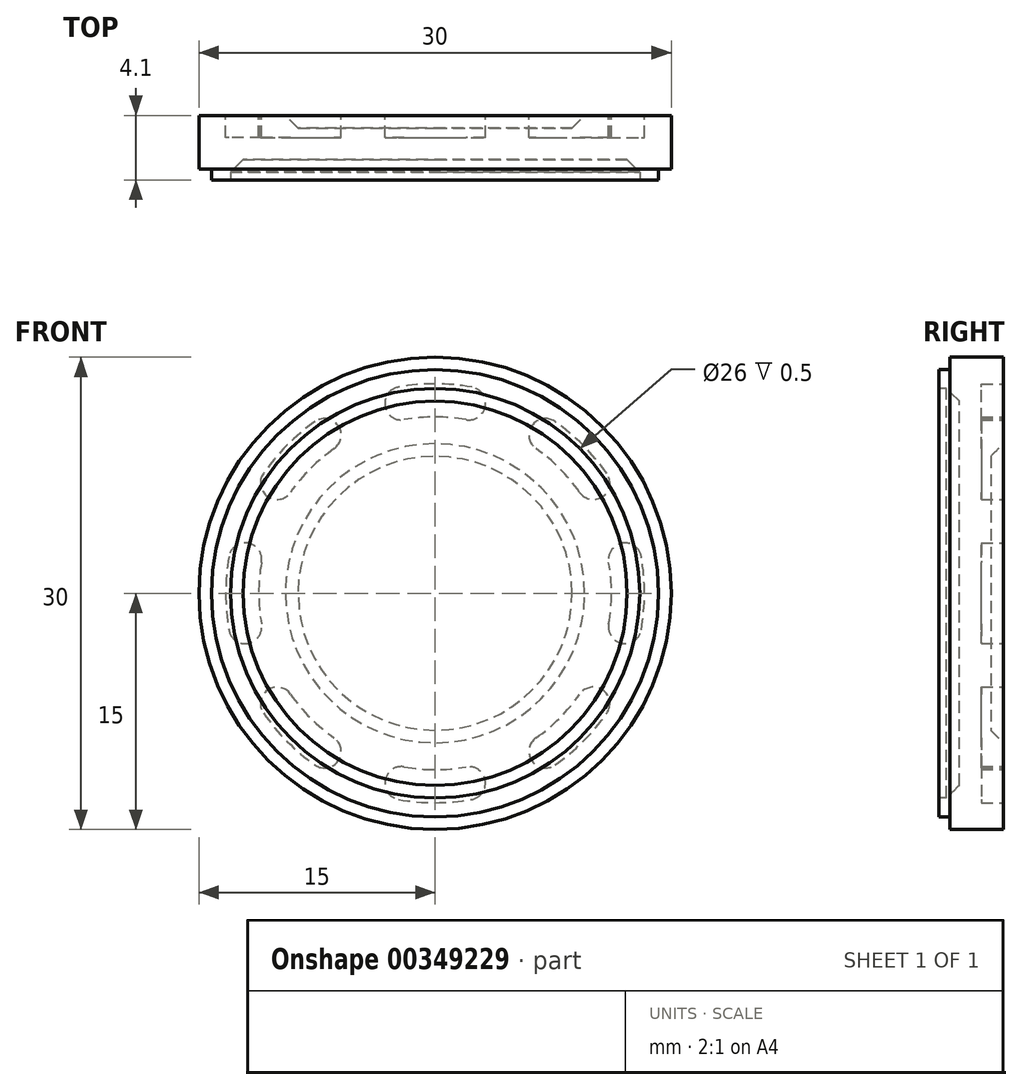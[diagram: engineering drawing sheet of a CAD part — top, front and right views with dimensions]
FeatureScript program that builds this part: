
annotation { "Feature Type Name" : "Feature", "Feature Type Description" : "" }
export const myFeature = defineFeature(function(context is Context, id is Id, definition is map)
    precondition{}
    {
        {
            var Q0;
            Q0=qCreatedBy(makeId("Front.planeOp"),FACE);
            var sketch = newSketch(context, id + "F0", { "sketchPlane" : qUnion([Q0])});
            skCircle(sketch, "E0", {"center": v(0, 0) * mm, "radius": 15 * mm});
            skCircle(sketch, "E1", {"center": v(0, 0) * mm, "radius": 9.5 * mm});
            skCircle(sketch, "E2", {"center": v(0, 0) * mm, "radius": 11.2 * mm});
            skCircle(sketch, "E3", {"center": v(0, 0) * mm, "radius": 13.3 * mm});
            skCircle(sketch, "E4", {"center": v(-12.06, 2.15) * mm, "radius": 1.05 * mm});
            skCircle(sketch, "E5", {"center": v(-12.06, -2.15) * mm, "radius": 1.05 * mm});
            skCircle(sketch, "E6.1.0", {"center": v(-10.05, -7.01) * mm, "radius": 1.05 * mm});
            skCircle(sketch, "E6.1.1", {"center": v(-7.01, -10.05) * mm, "radius": 1.05 * mm});
            skCircle(sketch, "E6.2.0", {"center": v(-2.15, -12.06) * mm, "radius": 1.05 * mm});
            skCircle(sketch, "E6.2.1", {"center": v(2.15, -12.06) * mm, "radius": 1.05 * mm});
            skCircle(sketch, "E7.1.3.0", {"center": v(7.01, -10.05) * mm, "radius": 1.05 * mm});
            skCircle(sketch, "E7.2.3.0", {"center": v(10.05, -7.01) * mm, "radius": 1.05 * mm});
            skCircle(sketch, "E7.1.4.0", {"center": v(12.06, -2.15) * mm, "radius": 1.05 * mm});
            skCircle(sketch, "E7.2.4.0", {"center": v(12.06, 2.15) * mm, "radius": 1.05 * mm});
            skCircle(sketch, "E7.1.5.0", {"center": v(10.05, 7.01) * mm, "radius": 1.05 * mm});
            skCircle(sketch, "E7.2.5.0", {"center": v(7.01, 10.05) * mm, "radius": 1.05 * mm});
            skCircle(sketch, "E7.1.6.0", {"center": v(2.15, 12.06) * mm, "radius": 1.05 * mm});
            skCircle(sketch, "E7.2.6.0", {"center": v(-2.15, 12.06) * mm, "radius": 1.05 * mm});
            skCircle(sketch, "E7.1.7.0", {"center": v(-7.01, 10.05) * mm, "radius": 1.05 * mm});
            skCircle(sketch, "E7.2.7.0", {"center": v(-10.05, 7.01) * mm, "radius": 1.05 * mm});
            skSolve(sketch);
        }
        {
            var Q0;
            Q0=qSketchRegion(id+"F0",true);
            var Q1;
            Q1=makeQuery(id+"F0.imprint","IMPRINT",FACE,{"disambiguationData":[TD([[makeQuery(id+"F0.imprint","IMPRINT",EDGE,{"derivedFrom":sQuery(id+"F0.wireOp",EDGE,"E1")}),1.0]])]});
            var Q2;
            {var subQ0=sQuery(id+"F0.wireOp",EDGE,"E2");var subQ1=sQuery(id+"F0.wireOp",EDGE,"vEkXL8x0-xW5C-LHgK-BDgQ-QKywttK1u6fH");var subQ2=makeQuery(id+"F0.imprint","INTERSECT",VERTEX,{"derivedFrom":[subQ1,subQ0]});Q2=makeQuery(id+"F0.imprint","IMPRINT",FACE,{"disambiguationData":[TD([[makeQuery(id+"F0.imprint","IMPRINT",EDGE,{"disambiguationData":[TD([[subQ2,1.0]])],"derivedFrom":subQ1}),-1.0]])]});}
            var Q3;
            {var subQ0=sQuery(id+"F0.wireOp",EDGE,"E2");var subQ1=sQuery(id+"F0.wireOp",EDGE,"6eb1e324-2513-47bc-ae3c-4e5281ed8811.10.0");var subQ2=makeQuery(id+"F0.imprint","INTERSECT",VERTEX,{"derivedFrom":[subQ1,subQ0]});Q3=makeQuery(id+"F0.imprint","IMPRINT",FACE,{"disambiguationData":[TD([[makeQuery(id+"F0.imprint","IMPRINT",EDGE,{"disambiguationData":[TD([[subQ2,1.0]])],"derivedFrom":subQ1}),-1.0]])]});}
            var Q4;
            {var subQ0=sQuery(id+"F0.wireOp",EDGE,"E2");var subQ1=sQuery(id+"F0.wireOp",EDGE,"6eb1e324-2513-47bc-ae3c-4e5281ed8811.8.0");var subQ2=makeQuery(id+"F0.imprint","INTERSECT",VERTEX,{"derivedFrom":[subQ1,subQ0]});Q4=makeQuery(id+"F0.imprint","IMPRINT",FACE,{"disambiguationData":[TD([[makeQuery(id+"F0.imprint","IMPRINT",EDGE,{"disambiguationData":[TD([[subQ2,1.0]])],"derivedFrom":subQ1}),-1.0]])]});}
            var Q5;
            {var subQ0=sQuery(id+"F0.wireOp",EDGE,"E2");var subQ1=sQuery(id+"F0.wireOp",EDGE,"6eb1e324-2513-47bc-ae3c-4e5281ed8811.6.0");var subQ2=makeQuery(id+"F0.imprint","INTERSECT",VERTEX,{"derivedFrom":[subQ1,subQ0]});Q5=makeQuery(id+"F0.imprint","IMPRINT",FACE,{"disambiguationData":[TD([[makeQuery(id+"F0.imprint","IMPRINT",EDGE,{"disambiguationData":[TD([[subQ2,1.0]])],"derivedFrom":subQ1}),-1.0]])]});}
            var Q6;
            {var subQ0=sQuery(id+"F0.wireOp",EDGE,"E2");var subQ1=sQuery(id+"F0.wireOp",EDGE,"6eb1e324-2513-47bc-ae3c-4e5281ed8811.4.0");var subQ2=makeQuery(id+"F0.imprint","INTERSECT",VERTEX,{"derivedFrom":[subQ1,subQ0]});Q6=makeQuery(id+"F0.imprint","IMPRINT",FACE,{"disambiguationData":[TD([[makeQuery(id+"F0.imprint","IMPRINT",EDGE,{"disambiguationData":[TD([[subQ2,1.0]])],"derivedFrom":subQ1}),-1.0]])]});}
            var Q7;
            {var subQ0=sQuery(id+"F0.wireOp",EDGE,"E2");var subQ1=sQuery(id+"F0.wireOp",EDGE,"6eb1e324-2513-47bc-ae3c-4e5281ed8811.2.0");var subQ2=makeQuery(id+"F0.imprint","INTERSECT",VERTEX,{"derivedFrom":[subQ1,subQ0]});Q7=makeQuery(id+"F0.imprint","IMPRINT",FACE,{"disambiguationData":[TD([[makeQuery(id+"F0.imprint","IMPRINT",EDGE,{"disambiguationData":[TD([[subQ2,1.0]])],"derivedFrom":subQ1}),-1.0]])]});}
            var Q8;
            Q8=makeQuery(id+"F0.imprint","IMPRINT",FACE,{"disambiguationData":[TD([[makeQuery(id+"F0.imprint","IMPRINT",EDGE,{"derivedFrom":sQuery(id+"F0.wireOp",EDGE,"E1")}),-1.0]])]});
            var Q9;
            {var subQ0=sQuery(id+"F0.wireOp",EDGE,"6eb1e324-2513-47bc-ae3c-4e5281ed8811.7.0");var subQ1=makeQuery(id+"F0.imprint","INTERSECT",VERTEX,{"derivedFrom":[subQ0,sQuery(id+"F0.wireOp",EDGE,"E2")]});Q9=makeQuery(id+"F0.imprint","IMPRINT",FACE,{"disambiguationData":[TD([[makeQuery(id+"F0.imprint","IMPRINT",EDGE,{"disambiguationData":[TD([[subQ1,1.0]])],"derivedFrom":subQ0}),1.0]])]});}
            var Q10;
            {var subQ0=sQuery(id+"F0.wireOp",EDGE,"E2");var subQ1=sQuery(id+"F0.wireOp",EDGE,"6eb1e324-2513-47bc-ae3c-4e5281ed8811.7.0");var subQ2=makeQuery(id+"F0.imprint","INTERSECT",VERTEX,{"derivedFrom":[subQ1,subQ0]});Q10=makeQuery(id+"F0.imprint","IMPRINT",FACE,{"disambiguationData":[TD([[makeQuery(id+"F0.imprint","IMPRINT",EDGE,{"disambiguationData":[TD([[subQ2,1.0]])],"derivedFrom":subQ1}),-1.0]])]});}
            var Q11;
            {var subQ0=sQuery(id+"F0.wireOp",EDGE,"6eb1e324-2513-47bc-ae3c-4e5281ed8811.8.0");var subQ1=makeQuery(id+"F0.imprint","INTERSECT",VERTEX,{"derivedFrom":[subQ0,sQuery(id+"F0.wireOp",EDGE,"E2")]});Q11=makeQuery(id+"F0.imprint","IMPRINT",FACE,{"disambiguationData":[TD([[makeQuery(id+"F0.imprint","IMPRINT",EDGE,{"disambiguationData":[TD([[subQ1,1.0]])],"derivedFrom":subQ0}),1.0]])]});}
            var Q12;
            {var subQ0=sQuery(id+"F0.wireOp",EDGE,"6eb1e324-2513-47bc-ae3c-4e5281ed8811.9.0");var subQ1=makeQuery(id+"F0.imprint","INTERSECT",VERTEX,{"derivedFrom":[subQ0,sQuery(id+"F0.wireOp",EDGE,"E2")]});Q12=makeQuery(id+"F0.imprint","IMPRINT",FACE,{"disambiguationData":[TD([[makeQuery(id+"F0.imprint","IMPRINT",EDGE,{"disambiguationData":[TD([[subQ1,1.0]])],"derivedFrom":subQ0}),1.0]])]});}
            var Q13;
            {var subQ0=sQuery(id+"F0.wireOp",EDGE,"E2");var subQ1=sQuery(id+"F0.wireOp",EDGE,"6eb1e324-2513-47bc-ae3c-4e5281ed8811.9.0");var subQ2=makeQuery(id+"F0.imprint","INTERSECT",VERTEX,{"derivedFrom":[subQ1,subQ0]});Q13=makeQuery(id+"F0.imprint","IMPRINT",FACE,{"disambiguationData":[TD([[makeQuery(id+"F0.imprint","IMPRINT",EDGE,{"disambiguationData":[TD([[subQ2,1.0]])],"derivedFrom":subQ1}),-1.0]])]});}
            var Q14;
            {var subQ0=sQuery(id+"F0.wireOp",EDGE,"6eb1e324-2513-47bc-ae3c-4e5281ed8811.10.0");var subQ1=makeQuery(id+"F0.imprint","INTERSECT",VERTEX,{"derivedFrom":[subQ0,sQuery(id+"F0.wireOp",EDGE,"E2")]});Q14=makeQuery(id+"F0.imprint","IMPRINT",FACE,{"disambiguationData":[TD([[makeQuery(id+"F0.imprint","IMPRINT",EDGE,{"disambiguationData":[TD([[subQ1,1.0]])],"derivedFrom":subQ0}),1.0]])]});}
            var Q15;
            {var subQ0=sQuery(id+"F0.wireOp",EDGE,"6eb1e324-2513-47bc-ae3c-4e5281ed8811.11.0");var subQ1=makeQuery(id+"F0.imprint","INTERSECT",VERTEX,{"derivedFrom":[subQ0,sQuery(id+"F0.wireOp",EDGE,"E2")]});Q15=makeQuery(id+"F0.imprint","IMPRINT",FACE,{"disambiguationData":[TD([[makeQuery(id+"F0.imprint","IMPRINT",EDGE,{"disambiguationData":[TD([[subQ1,1.0]])],"derivedFrom":subQ0}),1.0]])]});}
            var Q16;
            {var subQ0=sQuery(id+"F0.wireOp",EDGE,"E2");var subQ1=sQuery(id+"F0.wireOp",EDGE,"vEkXL8x0-xW5C-LHgK-BDgQ-QKywttK1u6fH");var subQ2=makeQuery(id+"F0.imprint","INTERSECT",VERTEX,{"derivedFrom":[subQ1,subQ0]});Q16=makeQuery(id+"F0.imprint","IMPRINT",FACE,{"disambiguationData":[TD([[makeQuery(id+"F0.imprint","IMPRINT",EDGE,{"disambiguationData":[TD([[subQ2,-1.0]])],"derivedFrom":subQ1}),-1.0]])]});}
            var Q17;
            {var subQ0=sQuery(id+"F0.wireOp",EDGE,"vEkXL8x0-xW5C-LHgK-BDgQ-QKywttK1u6fH");var subQ1=makeQuery(id+"F0.imprint","INTERSECT",VERTEX,{"derivedFrom":[subQ0,sQuery(id+"F0.wireOp",EDGE,"E2")]});Q17=makeQuery(id+"F0.imprint","IMPRINT",FACE,{"disambiguationData":[TD([[makeQuery(id+"F0.imprint","IMPRINT",EDGE,{"disambiguationData":[TD([[subQ1,1.0]])],"derivedFrom":subQ0}),1.0]])]});}
            var Q18;
            {var subQ0=sQuery(id+"F0.wireOp",EDGE,"6eb1e324-2513-47bc-ae3c-4e5281ed8811.1.0");var subQ1=makeQuery(id+"F0.imprint","INTERSECT",VERTEX,{"derivedFrom":[subQ0,sQuery(id+"F0.wireOp",EDGE,"E2")]});Q18=makeQuery(id+"F0.imprint","IMPRINT",FACE,{"disambiguationData":[TD([[makeQuery(id+"F0.imprint","IMPRINT",EDGE,{"disambiguationData":[TD([[subQ1,1.0]])],"derivedFrom":subQ0}),1.0]])]});}
            var Q19;
            {var subQ0=sQuery(id+"F0.wireOp",EDGE,"E2");var subQ1=sQuery(id+"F0.wireOp",EDGE,"6eb1e324-2513-47bc-ae3c-4e5281ed8811.1.0");var subQ2=makeQuery(id+"F0.imprint","INTERSECT",VERTEX,{"derivedFrom":[subQ1,subQ0]});Q19=makeQuery(id+"F0.imprint","IMPRINT",FACE,{"disambiguationData":[TD([[makeQuery(id+"F0.imprint","IMPRINT",EDGE,{"disambiguationData":[TD([[subQ2,1.0]])],"derivedFrom":subQ1}),-1.0]])]});}
            var Q20;
            {var subQ0=sQuery(id+"F0.wireOp",EDGE,"6eb1e324-2513-47bc-ae3c-4e5281ed8811.2.0");var subQ1=makeQuery(id+"F0.imprint","INTERSECT",VERTEX,{"derivedFrom":[subQ0,sQuery(id+"F0.wireOp",EDGE,"E2")]});Q20=makeQuery(id+"F0.imprint","IMPRINT",FACE,{"disambiguationData":[TD([[makeQuery(id+"F0.imprint","IMPRINT",EDGE,{"disambiguationData":[TD([[subQ1,1.0]])],"derivedFrom":subQ0}),1.0]])]});}
            var Q21;
            {var subQ0=sQuery(id+"F0.wireOp",EDGE,"6eb1e324-2513-47bc-ae3c-4e5281ed8811.3.0");var subQ1=makeQuery(id+"F0.imprint","INTERSECT",VERTEX,{"derivedFrom":[subQ0,sQuery(id+"F0.wireOp",EDGE,"E2")]});Q21=makeQuery(id+"F0.imprint","IMPRINT",FACE,{"disambiguationData":[TD([[makeQuery(id+"F0.imprint","IMPRINT",EDGE,{"disambiguationData":[TD([[subQ1,1.0]])],"derivedFrom":subQ0}),1.0]])]});}
            var Q22;
            {var subQ0=sQuery(id+"F0.wireOp",EDGE,"E2");var subQ1=sQuery(id+"F0.wireOp",EDGE,"6eb1e324-2513-47bc-ae3c-4e5281ed8811.3.0");var subQ2=makeQuery(id+"F0.imprint","INTERSECT",VERTEX,{"derivedFrom":[subQ1,subQ0]});Q22=makeQuery(id+"F0.imprint","IMPRINT",FACE,{"disambiguationData":[TD([[makeQuery(id+"F0.imprint","IMPRINT",EDGE,{"disambiguationData":[TD([[subQ2,1.0]])],"derivedFrom":subQ1}),-1.0]])]});}
            var Q23;
            {var subQ0=sQuery(id+"F0.wireOp",EDGE,"6eb1e324-2513-47bc-ae3c-4e5281ed8811.4.0");var subQ1=makeQuery(id+"F0.imprint","INTERSECT",VERTEX,{"derivedFrom":[subQ0,sQuery(id+"F0.wireOp",EDGE,"E2")]});Q23=makeQuery(id+"F0.imprint","IMPRINT",FACE,{"disambiguationData":[TD([[makeQuery(id+"F0.imprint","IMPRINT",EDGE,{"disambiguationData":[TD([[subQ1,1.0]])],"derivedFrom":subQ0}),1.0]])]});}
            var Q24;
            {var subQ0=sQuery(id+"F0.wireOp",EDGE,"6eb1e324-2513-47bc-ae3c-4e5281ed8811.5.0");var subQ1=makeQuery(id+"F0.imprint","INTERSECT",VERTEX,{"derivedFrom":[subQ0,sQuery(id+"F0.wireOp",EDGE,"E2")]});Q24=makeQuery(id+"F0.imprint","IMPRINT",FACE,{"disambiguationData":[TD([[makeQuery(id+"F0.imprint","IMPRINT",EDGE,{"disambiguationData":[TD([[subQ1,1.0]])],"derivedFrom":subQ0}),1.0]])]});}
            var Q25;
            {var subQ0=sQuery(id+"F0.wireOp",EDGE,"E2");var subQ1=sQuery(id+"F0.wireOp",EDGE,"6eb1e324-2513-47bc-ae3c-4e5281ed8811.5.0");var subQ2=makeQuery(id+"F0.imprint","INTERSECT",VERTEX,{"derivedFrom":[subQ1,subQ0]});Q25=makeQuery(id+"F0.imprint","IMPRINT",FACE,{"disambiguationData":[TD([[makeQuery(id+"F0.imprint","IMPRINT",EDGE,{"disambiguationData":[TD([[subQ2,1.0]])],"derivedFrom":subQ1}),-1.0]])]});}
            var Q26;
            {var subQ0=sQuery(id+"F0.wireOp",EDGE,"6eb1e324-2513-47bc-ae3c-4e5281ed8811.6.0");var subQ1=makeQuery(id+"F0.imprint","INTERSECT",VERTEX,{"derivedFrom":[subQ0,sQuery(id+"F0.wireOp",EDGE,"E2")]});Q26=makeQuery(id+"F0.imprint","IMPRINT",FACE,{"disambiguationData":[TD([[makeQuery(id+"F0.imprint","IMPRINT",EDGE,{"disambiguationData":[TD([[subQ1,1.0]])],"derivedFrom":subQ0}),1.0]])]});}
            var Q27;
            {var subQ0=sQuery(id+"F0.wireOp",EDGE,"d0c3eeaf-13b5-4f8c-83f5-547d6fbb3b3b.1.23.0");var subQ1=makeQuery(id+"F0.imprint","INTERSECT",VERTEX,{"derivedFrom":[sQuery(id+"F0.wireOp",EDGE,"E2"),subQ0]});Q27=makeQuery(id+"F0.imprint","IMPRINT",FACE,{"disambiguationData":[TD([[makeQuery(id+"F0.imprint","IMPRINT",EDGE,{"disambiguationData":[TD([[subQ1,1.0]])],"derivedFrom":subQ0}),1.0]])]});}
            var Q28;
            {var subQ0=sQuery(id+"F0.wireOp",EDGE,"d0c3eeaf-13b5-4f8c-83f5-547d6fbb3b3b.1.22.0");var subQ1=makeQuery(id+"F0.imprint","INTERSECT",VERTEX,{"derivedFrom":[sQuery(id+"F0.wireOp",EDGE,"E2"),subQ0]});Q28=makeQuery(id+"F0.imprint","IMPRINT",FACE,{"disambiguationData":[TD([[makeQuery(id+"F0.imprint","IMPRINT",EDGE,{"disambiguationData":[TD([[subQ1,1.0]])],"derivedFrom":subQ0}),1.0]])]});}
            var Q29;
            {var subQ0=sQuery(id+"F0.wireOp",EDGE,"d0c3eeaf-13b5-4f8c-83f5-547d6fbb3b3b.1.21.0");var subQ1=sQuery(id+"F0.wireOp",EDGE,"E2");var subQ2=makeQuery(id+"F0.imprint","INTERSECT",VERTEX,{"derivedFrom":[subQ1,subQ0]});Q29=makeQuery(id+"F0.imprint","IMPRINT",FACE,{"disambiguationData":[TD([[makeQuery(id+"F0.imprint","IMPRINT",EDGE,{"disambiguationData":[TD([[subQ2,-1.0]])],"derivedFrom":subQ1}),-1.0]])]});}
            var Q30;
            {var subQ0=sQuery(id+"F0.wireOp",EDGE,"d0c3eeaf-13b5-4f8c-83f5-547d6fbb3b3b.1.22.0");var subQ1=sQuery(id+"F0.wireOp",EDGE,"E2");var subQ2=makeQuery(id+"F0.imprint","INTERSECT",VERTEX,{"derivedFrom":[subQ1,subQ0]});Q30=makeQuery(id+"F0.imprint","IMPRINT",FACE,{"disambiguationData":[TD([[makeQuery(id+"F0.imprint","IMPRINT",EDGE,{"disambiguationData":[TD([[subQ2,-1.0]])],"derivedFrom":subQ1}),-1.0]])]});}
            var Q31;
            {var subQ0=sQuery(id+"F0.wireOp",EDGE,"d0c3eeaf-13b5-4f8c-83f5-547d6fbb3b3b.1.21.0");var subQ1=makeQuery(id+"F0.imprint","INTERSECT",VERTEX,{"derivedFrom":[sQuery(id+"F0.wireOp",EDGE,"E2"),subQ0]});Q31=makeQuery(id+"F0.imprint","IMPRINT",FACE,{"disambiguationData":[TD([[makeQuery(id+"F0.imprint","IMPRINT",EDGE,{"disambiguationData":[TD([[subQ1,1.0]])],"derivedFrom":subQ0}),1.0]])]});}
            var Q32;
            {var subQ0=sQuery(id+"F0.wireOp",EDGE,"d0c3eeaf-13b5-4f8c-83f5-547d6fbb3b3b.1.20.0");var subQ1=sQuery(id+"F0.wireOp",EDGE,"E2");var subQ2=makeQuery(id+"F0.imprint","INTERSECT",VERTEX,{"derivedFrom":[subQ1,subQ0]});Q32=makeQuery(id+"F0.imprint","IMPRINT",FACE,{"disambiguationData":[TD([[makeQuery(id+"F0.imprint","IMPRINT",EDGE,{"disambiguationData":[TD([[subQ2,-1.0]])],"derivedFrom":subQ1}),-1.0]])]});}
            var Q33;
            {var subQ0=sQuery(id+"F0.wireOp",EDGE,"d0c3eeaf-13b5-4f8c-83f5-547d6fbb3b3b.1.20.0");var subQ1=makeQuery(id+"F0.imprint","INTERSECT",VERTEX,{"derivedFrom":[sQuery(id+"F0.wireOp",EDGE,"E2"),subQ0]});Q33=makeQuery(id+"F0.imprint","IMPRINT",FACE,{"disambiguationData":[TD([[makeQuery(id+"F0.imprint","IMPRINT",EDGE,{"disambiguationData":[TD([[subQ1,1.0]])],"derivedFrom":subQ0}),1.0]])]});}
            var Q34;
            {var subQ0=sQuery(id+"F0.wireOp",EDGE,"d0c3eeaf-13b5-4f8c-83f5-547d6fbb3b3b.1.19.0");var subQ1=sQuery(id+"F0.wireOp",EDGE,"E2");var subQ2=makeQuery(id+"F0.imprint","INTERSECT",VERTEX,{"derivedFrom":[subQ1,subQ0]});Q34=makeQuery(id+"F0.imprint","IMPRINT",FACE,{"disambiguationData":[TD([[makeQuery(id+"F0.imprint","IMPRINT",EDGE,{"disambiguationData":[TD([[subQ2,-1.0]])],"derivedFrom":subQ1}),-1.0]])]});}
            var Q35;
            {var subQ0=sQuery(id+"F0.wireOp",EDGE,"d0c3eeaf-13b5-4f8c-83f5-547d6fbb3b3b.1.19.0");var subQ1=makeQuery(id+"F0.imprint","INTERSECT",VERTEX,{"derivedFrom":[sQuery(id+"F0.wireOp",EDGE,"E2"),subQ0]});Q35=makeQuery(id+"F0.imprint","IMPRINT",FACE,{"disambiguationData":[TD([[makeQuery(id+"F0.imprint","IMPRINT",EDGE,{"disambiguationData":[TD([[subQ1,1.0]])],"derivedFrom":subQ0}),1.0]])]});}
            var Q36;
            {var subQ0=sQuery(id+"F0.wireOp",EDGE,"d0c3eeaf-13b5-4f8c-83f5-547d6fbb3b3b.1.18.0");var subQ1=sQuery(id+"F0.wireOp",EDGE,"E2");var subQ2=makeQuery(id+"F0.imprint","INTERSECT",VERTEX,{"derivedFrom":[subQ1,subQ0]});Q36=makeQuery(id+"F0.imprint","IMPRINT",FACE,{"disambiguationData":[TD([[makeQuery(id+"F0.imprint","IMPRINT",EDGE,{"disambiguationData":[TD([[subQ2,-1.0]])],"derivedFrom":subQ1}),-1.0]])]});}
            var Q37;
            {var subQ0=sQuery(id+"F0.wireOp",EDGE,"d0c3eeaf-13b5-4f8c-83f5-547d6fbb3b3b.1.18.0");var subQ1=makeQuery(id+"F0.imprint","INTERSECT",VERTEX,{"derivedFrom":[sQuery(id+"F0.wireOp",EDGE,"E2"),subQ0]});Q37=makeQuery(id+"F0.imprint","IMPRINT",FACE,{"disambiguationData":[TD([[makeQuery(id+"F0.imprint","IMPRINT",EDGE,{"disambiguationData":[TD([[subQ1,1.0]])],"derivedFrom":subQ0}),1.0]])]});}
            var Q38;
            {var subQ0=sQuery(id+"F0.wireOp",EDGE,"d0c3eeaf-13b5-4f8c-83f5-547d6fbb3b3b.1.17.0");var subQ1=sQuery(id+"F0.wireOp",EDGE,"E2");var subQ2=makeQuery(id+"F0.imprint","INTERSECT",VERTEX,{"derivedFrom":[subQ1,subQ0]});Q38=makeQuery(id+"F0.imprint","IMPRINT",FACE,{"disambiguationData":[TD([[makeQuery(id+"F0.imprint","IMPRINT",EDGE,{"disambiguationData":[TD([[subQ2,-1.0]])],"derivedFrom":subQ1}),-1.0]])]});}
            var Q39;
            {var subQ0=sQuery(id+"F0.wireOp",EDGE,"d0c3eeaf-13b5-4f8c-83f5-547d6fbb3b3b.1.17.0");var subQ1=makeQuery(id+"F0.imprint","INTERSECT",VERTEX,{"derivedFrom":[sQuery(id+"F0.wireOp",EDGE,"E2"),subQ0]});Q39=makeQuery(id+"F0.imprint","IMPRINT",FACE,{"disambiguationData":[TD([[makeQuery(id+"F0.imprint","IMPRINT",EDGE,{"disambiguationData":[TD([[subQ1,1.0]])],"derivedFrom":subQ0}),1.0]])]});}
            var Q40;
            {var subQ0=sQuery(id+"F0.wireOp",EDGE,"d0c3eeaf-13b5-4f8c-83f5-547d6fbb3b3b.1.16.0");var subQ1=sQuery(id+"F0.wireOp",EDGE,"E2");var subQ2=makeQuery(id+"F0.imprint","INTERSECT",VERTEX,{"derivedFrom":[subQ1,subQ0]});Q40=makeQuery(id+"F0.imprint","IMPRINT",FACE,{"disambiguationData":[TD([[makeQuery(id+"F0.imprint","IMPRINT",EDGE,{"disambiguationData":[TD([[subQ2,-1.0]])],"derivedFrom":subQ1}),-1.0]])]});}
            var Q41;
            {var subQ0=sQuery(id+"F0.wireOp",EDGE,"d0c3eeaf-13b5-4f8c-83f5-547d6fbb3b3b.1.16.0");var subQ1=makeQuery(id+"F0.imprint","INTERSECT",VERTEX,{"derivedFrom":[sQuery(id+"F0.wireOp",EDGE,"E2"),subQ0]});Q41=makeQuery(id+"F0.imprint","IMPRINT",FACE,{"disambiguationData":[TD([[makeQuery(id+"F0.imprint","IMPRINT",EDGE,{"disambiguationData":[TD([[subQ1,1.0]])],"derivedFrom":subQ0}),1.0]])]});}
            var Q42;
            {var subQ0=sQuery(id+"F0.wireOp",EDGE,"d0c3eeaf-13b5-4f8c-83f5-547d6fbb3b3b.1.15.0");var subQ1=sQuery(id+"F0.wireOp",EDGE,"E2");var subQ2=makeQuery(id+"F0.imprint","INTERSECT",VERTEX,{"derivedFrom":[subQ1,subQ0]});Q42=makeQuery(id+"F0.imprint","IMPRINT",FACE,{"disambiguationData":[TD([[makeQuery(id+"F0.imprint","IMPRINT",EDGE,{"disambiguationData":[TD([[subQ2,-1.0]])],"derivedFrom":subQ1}),-1.0]])]});}
            var Q43;
            {var subQ0=sQuery(id+"F0.wireOp",EDGE,"d0c3eeaf-13b5-4f8c-83f5-547d6fbb3b3b.1.15.0");var subQ1=makeQuery(id+"F0.imprint","INTERSECT",VERTEX,{"derivedFrom":[sQuery(id+"F0.wireOp",EDGE,"E2"),subQ0]});Q43=makeQuery(id+"F0.imprint","IMPRINT",FACE,{"disambiguationData":[TD([[makeQuery(id+"F0.imprint","IMPRINT",EDGE,{"disambiguationData":[TD([[subQ1,1.0]])],"derivedFrom":subQ0}),1.0]])]});}
            var Q44;
            {var subQ0=sQuery(id+"F0.wireOp",EDGE,"d0c3eeaf-13b5-4f8c-83f5-547d6fbb3b3b.1.14.0");var subQ1=sQuery(id+"F0.wireOp",EDGE,"E2");var subQ2=makeQuery(id+"F0.imprint","INTERSECT",VERTEX,{"derivedFrom":[subQ1,subQ0]});Q44=makeQuery(id+"F0.imprint","IMPRINT",FACE,{"disambiguationData":[TD([[makeQuery(id+"F0.imprint","IMPRINT",EDGE,{"disambiguationData":[TD([[subQ2,-1.0]])],"derivedFrom":subQ1}),-1.0]])]});}
            var Q45;
            {var subQ0=sQuery(id+"F0.wireOp",EDGE,"d0c3eeaf-13b5-4f8c-83f5-547d6fbb3b3b.1.14.0");var subQ1=makeQuery(id+"F0.imprint","INTERSECT",VERTEX,{"derivedFrom":[sQuery(id+"F0.wireOp",EDGE,"E2"),subQ0]});Q45=makeQuery(id+"F0.imprint","IMPRINT",FACE,{"disambiguationData":[TD([[makeQuery(id+"F0.imprint","IMPRINT",EDGE,{"disambiguationData":[TD([[subQ1,1.0]])],"derivedFrom":subQ0}),1.0]])]});}
            var Q46;
            {var subQ0=sQuery(id+"F0.wireOp",EDGE,"d0c3eeaf-13b5-4f8c-83f5-547d6fbb3b3b.1.13.0");var subQ1=sQuery(id+"F0.wireOp",EDGE,"E2");var subQ2=makeQuery(id+"F0.imprint","INTERSECT",VERTEX,{"derivedFrom":[subQ1,subQ0]});Q46=makeQuery(id+"F0.imprint","IMPRINT",FACE,{"disambiguationData":[TD([[makeQuery(id+"F0.imprint","IMPRINT",EDGE,{"disambiguationData":[TD([[subQ2,-1.0]])],"derivedFrom":subQ1}),-1.0]])]});}
            var Q47;
            {var subQ0=sQuery(id+"F0.wireOp",EDGE,"d0c3eeaf-13b5-4f8c-83f5-547d6fbb3b3b.1.13.0");var subQ1=makeQuery(id+"F0.imprint","INTERSECT",VERTEX,{"derivedFrom":[sQuery(id+"F0.wireOp",EDGE,"E2"),subQ0]});Q47=makeQuery(id+"F0.imprint","IMPRINT",FACE,{"disambiguationData":[TD([[makeQuery(id+"F0.imprint","IMPRINT",EDGE,{"disambiguationData":[TD([[subQ1,1.0]])],"derivedFrom":subQ0}),1.0]])]});}
            var Q48;
            {var subQ0=sQuery(id+"F0.wireOp",EDGE,"d0c3eeaf-13b5-4f8c-83f5-547d6fbb3b3b.1.12.0");var subQ1=sQuery(id+"F0.wireOp",EDGE,"E2");var subQ2=makeQuery(id+"F0.imprint","INTERSECT",VERTEX,{"derivedFrom":[subQ1,subQ0]});Q48=makeQuery(id+"F0.imprint","IMPRINT",FACE,{"disambiguationData":[TD([[makeQuery(id+"F0.imprint","IMPRINT",EDGE,{"disambiguationData":[TD([[subQ2,-1.0]])],"derivedFrom":subQ1}),-1.0]])]});}
            var Q49;
            {var subQ0=sQuery(id+"F0.wireOp",EDGE,"d0c3eeaf-13b5-4f8c-83f5-547d6fbb3b3b.1.12.0");var subQ1=makeQuery(id+"F0.imprint","INTERSECT",VERTEX,{"derivedFrom":[sQuery(id+"F0.wireOp",EDGE,"E2"),subQ0]});Q49=makeQuery(id+"F0.imprint","IMPRINT",FACE,{"disambiguationData":[TD([[makeQuery(id+"F0.imprint","IMPRINT",EDGE,{"disambiguationData":[TD([[subQ1,1.0]])],"derivedFrom":subQ0}),1.0]])]});}
            var Q50;
            {var subQ0=sQuery(id+"F0.wireOp",EDGE,"E2");var subQ1=sQuery(id+"F0.wireOp",EDGE,"6eb1e324-2513-47bc-ae3c-4e5281ed8811.11.0");var subQ2=makeQuery(id+"F0.imprint","INTERSECT",VERTEX,{"derivedFrom":[subQ1,subQ0]});Q50=makeQuery(id+"F0.imprint","IMPRINT",FACE,{"disambiguationData":[TD([[makeQuery(id+"F0.imprint","IMPRINT",EDGE,{"disambiguationData":[TD([[subQ2,1.0]])],"derivedFrom":subQ1}),-1.0]])]});}
            var Q51;
            {var subQ0=sQuery(id+"F0.wireOp",EDGE,"E5");var subQ1=makeQuery(id+"F0.imprint","INTERSECT",VERTEX,{"derivedFrom":[sQuery(id+"F0.wireOp",EDGE,"E2"),subQ0]});Q51=makeQuery(id+"F0.imprint","IMPRINT",FACE,{"disambiguationData":[TD([[makeQuery(id+"F0.imprint","IMPRINT",EDGE,{"disambiguationData":[TD([[subQ1,-1.0]])],"derivedFrom":subQ0}),1.0]])]});}
            var Q52;
            {var subQ0=sQuery(id+"F0.wireOp",EDGE,"E4");var subQ1=makeQuery(id+"F0.imprint","INTERSECT",VERTEX,{"derivedFrom":[sQuery(id+"F0.wireOp",EDGE,"E2"),subQ0]});Q52=makeQuery(id+"F0.imprint","IMPRINT",FACE,{"disambiguationData":[TD([[makeQuery(id+"F0.imprint","IMPRINT",EDGE,{"disambiguationData":[TD([[subQ1,1.0]])],"derivedFrom":subQ0}),1.0]])]});}
            var Q53;
            {var subQ0=sQuery(id+"F0.wireOp",EDGE,"E6.1.0");var subQ1=makeQuery(id+"F0.imprint","INTERSECT",VERTEX,{"derivedFrom":[sQuery(id+"F0.wireOp",EDGE,"E2"),subQ0]});Q53=makeQuery(id+"F0.imprint","IMPRINT",FACE,{"disambiguationData":[TD([[makeQuery(id+"F0.imprint","IMPRINT",EDGE,{"disambiguationData":[TD([[subQ1,1.0]])],"derivedFrom":subQ0}),1.0]])]});}
            var Q54;
            {var subQ0=sQuery(id+"F0.wireOp",EDGE,"E6.1.1");var subQ1=makeQuery(id+"F0.imprint","INTERSECT",VERTEX,{"derivedFrom":[sQuery(id+"F0.wireOp",EDGE,"E2"),subQ0]});Q54=makeQuery(id+"F0.imprint","IMPRINT",FACE,{"disambiguationData":[TD([[makeQuery(id+"F0.imprint","IMPRINT",EDGE,{"disambiguationData":[TD([[subQ1,-1.0]])],"derivedFrom":subQ0}),1.0]])]});}
            var Q55;
            {var subQ0=sQuery(id+"F0.wireOp",EDGE,"E6.2.0");var subQ1=makeQuery(id+"F0.imprint","INTERSECT",VERTEX,{"derivedFrom":[sQuery(id+"F0.wireOp",EDGE,"E2"),subQ0]});Q55=makeQuery(id+"F0.imprint","IMPRINT",FACE,{"disambiguationData":[TD([[makeQuery(id+"F0.imprint","IMPRINT",EDGE,{"disambiguationData":[TD([[subQ1,1.0]])],"derivedFrom":subQ0}),1.0]])]});}
            var Q56;
            {var subQ0=sQuery(id+"F0.wireOp",EDGE,"E6.2.1");var subQ1=makeQuery(id+"F0.imprint","INTERSECT",VERTEX,{"derivedFrom":[sQuery(id+"F0.wireOp",EDGE,"E2"),subQ0]});Q56=makeQuery(id+"F0.imprint","IMPRINT",FACE,{"disambiguationData":[TD([[makeQuery(id+"F0.imprint","IMPRINT",EDGE,{"disambiguationData":[TD([[subQ1,-1.0]])],"derivedFrom":subQ0}),1.0]])]});}
            var Q57;
            {var subQ0=sQuery(id+"F0.wireOp",EDGE,"E7.1.3.0");var subQ1=makeQuery(id+"F0.imprint","INTERSECT",VERTEX,{"derivedFrom":[sQuery(id+"F0.wireOp",EDGE,"E2"),subQ0]});Q57=makeQuery(id+"F0.imprint","IMPRINT",FACE,{"disambiguationData":[TD([[makeQuery(id+"F0.imprint","IMPRINT",EDGE,{"disambiguationData":[TD([[subQ1,1.0]])],"derivedFrom":subQ0}),1.0]])]});}
            var Q58;
            {var subQ0=sQuery(id+"F0.wireOp",EDGE,"E7.2.3.0");var subQ1=makeQuery(id+"F0.imprint","INTERSECT",VERTEX,{"derivedFrom":[sQuery(id+"F0.wireOp",EDGE,"E2"),subQ0]});Q58=makeQuery(id+"F0.imprint","IMPRINT",FACE,{"disambiguationData":[TD([[makeQuery(id+"F0.imprint","IMPRINT",EDGE,{"disambiguationData":[TD([[subQ1,-1.0]])],"derivedFrom":subQ0}),1.0]])]});}
            var Q59;
            {var subQ0=sQuery(id+"F0.wireOp",EDGE,"E7.1.4.0");var subQ1=makeQuery(id+"F0.imprint","INTERSECT",VERTEX,{"derivedFrom":[sQuery(id+"F0.wireOp",EDGE,"E2"),subQ0]});Q59=makeQuery(id+"F0.imprint","IMPRINT",FACE,{"disambiguationData":[TD([[makeQuery(id+"F0.imprint","IMPRINT",EDGE,{"disambiguationData":[TD([[subQ1,1.0]])],"derivedFrom":subQ0}),1.0]])]});}
            var Q60;
            {var subQ0=sQuery(id+"F0.wireOp",EDGE,"E7.2.4.0");var subQ1=makeQuery(id+"F0.imprint","INTERSECT",VERTEX,{"derivedFrom":[sQuery(id+"F0.wireOp",EDGE,"E2"),subQ0]});Q60=makeQuery(id+"F0.imprint","IMPRINT",FACE,{"disambiguationData":[TD([[makeQuery(id+"F0.imprint","IMPRINT",EDGE,{"disambiguationData":[TD([[subQ1,-1.0]])],"derivedFrom":subQ0}),1.0]])]});}
            var Q61;
            {var subQ0=sQuery(id+"F0.wireOp",EDGE,"E7.1.5.0");var subQ1=makeQuery(id+"F0.imprint","INTERSECT",VERTEX,{"derivedFrom":[sQuery(id+"F0.wireOp",EDGE,"E2"),subQ0]});Q61=makeQuery(id+"F0.imprint","IMPRINT",FACE,{"disambiguationData":[TD([[makeQuery(id+"F0.imprint","IMPRINT",EDGE,{"disambiguationData":[TD([[subQ1,1.0]])],"derivedFrom":subQ0}),1.0]])]});}
            var Q62;
            {var subQ0=sQuery(id+"F0.wireOp",EDGE,"E7.2.7.0");var subQ1=makeQuery(id+"F0.imprint","INTERSECT",VERTEX,{"derivedFrom":[sQuery(id+"F0.wireOp",EDGE,"E2"),subQ0]});Q62=makeQuery(id+"F0.imprint","IMPRINT",FACE,{"disambiguationData":[TD([[makeQuery(id+"F0.imprint","IMPRINT",EDGE,{"disambiguationData":[TD([[subQ1,-1.0]])],"derivedFrom":subQ0}),1.0]])]});}
            var Q63;
            {var subQ0=sQuery(id+"F0.wireOp",EDGE,"E7.1.7.0");var subQ1=makeQuery(id+"F0.imprint","INTERSECT",VERTEX,{"derivedFrom":[sQuery(id+"F0.wireOp",EDGE,"E2"),subQ0]});Q63=makeQuery(id+"F0.imprint","IMPRINT",FACE,{"disambiguationData":[TD([[makeQuery(id+"F0.imprint","IMPRINT",EDGE,{"disambiguationData":[TD([[subQ1,1.0]])],"derivedFrom":subQ0}),1.0]])]});}
            var Q64;
            {var subQ0=sQuery(id+"F0.wireOp",EDGE,"E7.2.6.0");var subQ1=makeQuery(id+"F0.imprint","INTERSECT",VERTEX,{"derivedFrom":[sQuery(id+"F0.wireOp",EDGE,"E2"),subQ0]});Q64=makeQuery(id+"F0.imprint","IMPRINT",FACE,{"disambiguationData":[TD([[makeQuery(id+"F0.imprint","IMPRINT",EDGE,{"disambiguationData":[TD([[subQ1,-1.0]])],"derivedFrom":subQ0}),1.0]])]});}
            var Q65;
            {var subQ0=sQuery(id+"F0.wireOp",EDGE,"E7.1.6.0");var subQ1=makeQuery(id+"F0.imprint","INTERSECT",VERTEX,{"derivedFrom":[sQuery(id+"F0.wireOp",EDGE,"E2"),subQ0]});Q65=makeQuery(id+"F0.imprint","IMPRINT",FACE,{"disambiguationData":[TD([[makeQuery(id+"F0.imprint","IMPRINT",EDGE,{"disambiguationData":[TD([[subQ1,1.0]])],"derivedFrom":subQ0}),1.0]])]});}
            var Q66;
            {var subQ0=sQuery(id+"F0.wireOp",EDGE,"E7.2.5.0");var subQ1=makeQuery(id+"F0.imprint","INTERSECT",VERTEX,{"derivedFrom":[sQuery(id+"F0.wireOp",EDGE,"E2"),subQ0]});Q66=makeQuery(id+"F0.imprint","IMPRINT",FACE,{"disambiguationData":[TD([[makeQuery(id+"F0.imprint","IMPRINT",EDGE,{"disambiguationData":[TD([[subQ1,-1.0]])],"derivedFrom":subQ0}),1.0]])]});}
            extrude(context, id + "F1", {"entities" : qUnion([Q0, Q1, Q2, Q3, Q4, Q5, Q6, Q7, Q8, Q9, Q10, Q11, Q12, Q13, Q14, Q15, Q16, Q17, Q18, Q19, Q20, Q21, Q22, Q23, Q24, Q25, Q26, Q27, Q28, Q29, Q30, Q31, Q32, Q33, Q34, Q35, Q36, Q37, Q38, Q39, Q40, Q41, Q42, Q43, Q44, Q45, Q46, Q47, Q48, Q49, Q50, Q51, Q52, Q53, Q54, Q55, Q56, Q57, Q58, Q59, Q60, Q61, Q62, Q63, Q64, Q65, Q66]), "depth" : 4.1 * mm});
        }
        {
            var Q0;
            {var subQ0=sQuery(id+"F0.wireOp",EDGE,"E6.2.0");var subQ1=sQuery(id+"F0.wireOp",EDGE,"E2");var subQ2=makeQuery(id+"F0.imprint","INTERSECT",VERTEX,{"derivedFrom":[subQ1,subQ0]});Q0=makeQuery(id+"F0.imprint","IMPRINT",FACE,{"disambiguationData":[TD([[makeQuery(id+"F0.imprint","IMPRINT",EDGE,{"disambiguationData":[TD([[subQ2,-1.0]])],"derivedFrom":subQ1}),-1.0]])]});}
            var Q1;
            {var subQ0=sQuery(id+"F0.wireOp",EDGE,"E7.1.3.0");var subQ1=sQuery(id+"F0.wireOp",EDGE,"E2");var subQ2=makeQuery(id+"F0.imprint","INTERSECT",VERTEX,{"derivedFrom":[subQ1,subQ0]});Q1=makeQuery(id+"F0.imprint","IMPRINT",FACE,{"disambiguationData":[TD([[makeQuery(id+"F0.imprint","IMPRINT",EDGE,{"disambiguationData":[TD([[subQ2,-1.0]])],"derivedFrom":subQ1}),-1.0]])]});}
            var Q2;
            {var subQ0=sQuery(id+"F0.wireOp",EDGE,"E7.2.4.0");var subQ1=sQuery(id+"F0.wireOp",EDGE,"E2");var subQ2=makeQuery(id+"F0.imprint","INTERSECT",VERTEX,{"derivedFrom":[subQ1,subQ0]});Q2=makeQuery(id+"F0.imprint","IMPRINT",FACE,{"disambiguationData":[TD([[makeQuery(id+"F0.imprint","IMPRINT",EDGE,{"disambiguationData":[TD([[subQ2,1.0]])],"derivedFrom":subQ1}),-1.0]])]});}
            var Q3;
            {var subQ0=sQuery(id+"F0.wireOp",EDGE,"E4");var subQ1=sQuery(id+"F0.wireOp",EDGE,"E2");var subQ2=makeQuery(id+"F0.imprint","INTERSECT",VERTEX,{"derivedFrom":[subQ1,subQ0]});Q3=makeQuery(id+"F0.imprint","IMPRINT",FACE,{"disambiguationData":[TD([[makeQuery(id+"F0.imprint","IMPRINT",EDGE,{"disambiguationData":[TD([[subQ2,-1.0]])],"derivedFrom":subQ1}),-1.0]])]});}
            var Q4;
            {var subQ0=sQuery(id+"F0.wireOp",EDGE,"E6.1.0");var subQ1=sQuery(id+"F0.wireOp",EDGE,"E2");var subQ2=makeQuery(id+"F0.imprint","INTERSECT",VERTEX,{"derivedFrom":[subQ1,subQ0]});Q4=makeQuery(id+"F0.imprint","IMPRINT",FACE,{"disambiguationData":[TD([[makeQuery(id+"F0.imprint","IMPRINT",EDGE,{"disambiguationData":[TD([[subQ2,-1.0]])],"derivedFrom":subQ1}),-1.0]])]});}
            var Q5;
            {var subQ0=sQuery(id+"F0.wireOp",EDGE,"E7.1.7.0");var subQ1=sQuery(id+"F0.wireOp",EDGE,"E2");var subQ2=makeQuery(id+"F0.imprint","INTERSECT",VERTEX,{"derivedFrom":[subQ1,subQ0]});Q5=makeQuery(id+"F0.imprint","IMPRINT",FACE,{"disambiguationData":[TD([[makeQuery(id+"F0.imprint","IMPRINT",EDGE,{"disambiguationData":[TD([[subQ2,-1.0]])],"derivedFrom":subQ1}),-1.0]])]});}
            var Q6;
            {var subQ0=sQuery(id+"F0.wireOp",EDGE,"E7.1.6.0");var subQ1=sQuery(id+"F0.wireOp",EDGE,"E2");var subQ2=makeQuery(id+"F0.imprint","INTERSECT",VERTEX,{"derivedFrom":[subQ1,subQ0]});Q6=makeQuery(id+"F0.imprint","IMPRINT",FACE,{"disambiguationData":[TD([[makeQuery(id+"F0.imprint","IMPRINT",EDGE,{"disambiguationData":[TD([[subQ2,-1.0]])],"derivedFrom":subQ1}),-1.0]])]});}
            var Q7;
            {var subQ0=sQuery(id+"F0.wireOp",EDGE,"E7.1.5.0");var subQ1=sQuery(id+"F0.wireOp",EDGE,"E2");var subQ2=makeQuery(id+"F0.imprint","INTERSECT",VERTEX,{"derivedFrom":[subQ1,subQ0]});Q7=makeQuery(id+"F0.imprint","IMPRINT",FACE,{"disambiguationData":[TD([[makeQuery(id+"F0.imprint","IMPRINT",EDGE,{"disambiguationData":[TD([[subQ2,-1.0]])],"derivedFrom":subQ1}),-1.0]])]});}
            var Q8;
            {var subQ0=sQuery(id+"F0.wireOp",EDGE,"E5");var subQ1=makeQuery(id+"F0.imprint","INTERSECT",VERTEX,{"derivedFrom":[sQuery(id+"F0.wireOp",EDGE,"E2"),subQ0]});Q8=makeQuery(id+"F0.imprint","IMPRINT",FACE,{"disambiguationData":[TD([[makeQuery(id+"F0.imprint","IMPRINT",EDGE,{"disambiguationData":[TD([[subQ1,-1.0]])],"derivedFrom":subQ0}),1.0]])]});}
            var Q9;
            {var subQ0=sQuery(id+"F0.wireOp",EDGE,"E6.1.0");var subQ1=makeQuery(id+"F0.imprint","INTERSECT",VERTEX,{"derivedFrom":[sQuery(id+"F0.wireOp",EDGE,"E2"),subQ0]});Q9=makeQuery(id+"F0.imprint","IMPRINT",FACE,{"disambiguationData":[TD([[makeQuery(id+"F0.imprint","IMPRINT",EDGE,{"disambiguationData":[TD([[subQ1,1.0]])],"derivedFrom":subQ0}),1.0]])]});}
            var Q10;
            {var subQ0=sQuery(id+"F0.wireOp",EDGE,"E6.1.1");var subQ1=makeQuery(id+"F0.imprint","INTERSECT",VERTEX,{"derivedFrom":[sQuery(id+"F0.wireOp",EDGE,"E2"),subQ0]});Q10=makeQuery(id+"F0.imprint","IMPRINT",FACE,{"disambiguationData":[TD([[makeQuery(id+"F0.imprint","IMPRINT",EDGE,{"disambiguationData":[TD([[subQ1,-1.0]])],"derivedFrom":subQ0}),1.0]])]});}
            var Q11;
            {var subQ0=sQuery(id+"F0.wireOp",EDGE,"E6.2.0");var subQ1=makeQuery(id+"F0.imprint","INTERSECT",VERTEX,{"derivedFrom":[sQuery(id+"F0.wireOp",EDGE,"E2"),subQ0]});Q11=makeQuery(id+"F0.imprint","IMPRINT",FACE,{"disambiguationData":[TD([[makeQuery(id+"F0.imprint","IMPRINT",EDGE,{"disambiguationData":[TD([[subQ1,1.0]])],"derivedFrom":subQ0}),1.0]])]});}
            var Q12;
            {var subQ0=sQuery(id+"F0.wireOp",EDGE,"E6.2.1");var subQ1=makeQuery(id+"F0.imprint","INTERSECT",VERTEX,{"derivedFrom":[sQuery(id+"F0.wireOp",EDGE,"E2"),subQ0]});Q12=makeQuery(id+"F0.imprint","IMPRINT",FACE,{"disambiguationData":[TD([[makeQuery(id+"F0.imprint","IMPRINT",EDGE,{"disambiguationData":[TD([[subQ1,-1.0]])],"derivedFrom":subQ0}),1.0]])]});}
            var Q13;
            {var subQ0=sQuery(id+"F0.wireOp",EDGE,"E7.1.3.0");var subQ1=makeQuery(id+"F0.imprint","INTERSECT",VERTEX,{"derivedFrom":[sQuery(id+"F0.wireOp",EDGE,"E2"),subQ0]});Q13=makeQuery(id+"F0.imprint","IMPRINT",FACE,{"disambiguationData":[TD([[makeQuery(id+"F0.imprint","IMPRINT",EDGE,{"disambiguationData":[TD([[subQ1,1.0]])],"derivedFrom":subQ0}),1.0]])]});}
            var Q14;
            {var subQ0=sQuery(id+"F0.wireOp",EDGE,"E7.2.3.0");var subQ1=makeQuery(id+"F0.imprint","INTERSECT",VERTEX,{"derivedFrom":[sQuery(id+"F0.wireOp",EDGE,"E2"),subQ0]});Q14=makeQuery(id+"F0.imprint","IMPRINT",FACE,{"disambiguationData":[TD([[makeQuery(id+"F0.imprint","IMPRINT",EDGE,{"disambiguationData":[TD([[subQ1,-1.0]])],"derivedFrom":subQ0}),1.0]])]});}
            var Q15;
            {var subQ0=sQuery(id+"F0.wireOp",EDGE,"E7.1.4.0");var subQ1=makeQuery(id+"F0.imprint","INTERSECT",VERTEX,{"derivedFrom":[sQuery(id+"F0.wireOp",EDGE,"E2"),subQ0]});Q15=makeQuery(id+"F0.imprint","IMPRINT",FACE,{"disambiguationData":[TD([[makeQuery(id+"F0.imprint","IMPRINT",EDGE,{"disambiguationData":[TD([[subQ1,1.0]])],"derivedFrom":subQ0}),1.0]])]});}
            var Q16;
            {var subQ0=sQuery(id+"F0.wireOp",EDGE,"E7.2.4.0");var subQ1=makeQuery(id+"F0.imprint","INTERSECT",VERTEX,{"derivedFrom":[sQuery(id+"F0.wireOp",EDGE,"E2"),subQ0]});Q16=makeQuery(id+"F0.imprint","IMPRINT",FACE,{"disambiguationData":[TD([[makeQuery(id+"F0.imprint","IMPRINT",EDGE,{"disambiguationData":[TD([[subQ1,-1.0]])],"derivedFrom":subQ0}),1.0]])]});}
            var Q17;
            {var subQ0=sQuery(id+"F0.wireOp",EDGE,"E7.1.5.0");var subQ1=makeQuery(id+"F0.imprint","INTERSECT",VERTEX,{"derivedFrom":[sQuery(id+"F0.wireOp",EDGE,"E2"),subQ0]});Q17=makeQuery(id+"F0.imprint","IMPRINT",FACE,{"disambiguationData":[TD([[makeQuery(id+"F0.imprint","IMPRINT",EDGE,{"disambiguationData":[TD([[subQ1,1.0]])],"derivedFrom":subQ0}),1.0]])]});}
            var Q18;
            {var subQ0=sQuery(id+"F0.wireOp",EDGE,"E7.2.5.0");var subQ1=makeQuery(id+"F0.imprint","INTERSECT",VERTEX,{"derivedFrom":[sQuery(id+"F0.wireOp",EDGE,"E2"),subQ0]});Q18=makeQuery(id+"F0.imprint","IMPRINT",FACE,{"disambiguationData":[TD([[makeQuery(id+"F0.imprint","IMPRINT",EDGE,{"disambiguationData":[TD([[subQ1,-1.0]])],"derivedFrom":subQ0}),1.0]])]});}
            var Q19;
            {var subQ0=sQuery(id+"F0.wireOp",EDGE,"E7.1.6.0");var subQ1=makeQuery(id+"F0.imprint","INTERSECT",VERTEX,{"derivedFrom":[sQuery(id+"F0.wireOp",EDGE,"E2"),subQ0]});Q19=makeQuery(id+"F0.imprint","IMPRINT",FACE,{"disambiguationData":[TD([[makeQuery(id+"F0.imprint","IMPRINT",EDGE,{"disambiguationData":[TD([[subQ1,1.0]])],"derivedFrom":subQ0}),1.0]])]});}
            var Q20;
            {var subQ0=sQuery(id+"F0.wireOp",EDGE,"E7.2.6.0");var subQ1=makeQuery(id+"F0.imprint","INTERSECT",VERTEX,{"derivedFrom":[sQuery(id+"F0.wireOp",EDGE,"E2"),subQ0]});Q20=makeQuery(id+"F0.imprint","IMPRINT",FACE,{"disambiguationData":[TD([[makeQuery(id+"F0.imprint","IMPRINT",EDGE,{"disambiguationData":[TD([[subQ1,-1.0]])],"derivedFrom":subQ0}),1.0]])]});}
            var Q21;
            {var subQ0=sQuery(id+"F0.wireOp",EDGE,"E7.1.7.0");var subQ1=makeQuery(id+"F0.imprint","INTERSECT",VERTEX,{"derivedFrom":[sQuery(id+"F0.wireOp",EDGE,"E2"),subQ0]});Q21=makeQuery(id+"F0.imprint","IMPRINT",FACE,{"disambiguationData":[TD([[makeQuery(id+"F0.imprint","IMPRINT",EDGE,{"disambiguationData":[TD([[subQ1,1.0]])],"derivedFrom":subQ0}),1.0]])]});}
            var Q22;
            {var subQ0=sQuery(id+"F0.wireOp",EDGE,"E7.2.7.0");var subQ1=makeQuery(id+"F0.imprint","INTERSECT",VERTEX,{"derivedFrom":[sQuery(id+"F0.wireOp",EDGE,"E2"),subQ0]});Q22=makeQuery(id+"F0.imprint","IMPRINT",FACE,{"disambiguationData":[TD([[makeQuery(id+"F0.imprint","IMPRINT",EDGE,{"disambiguationData":[TD([[subQ1,-1.0]])],"derivedFrom":subQ0}),1.0]])]});}
            var Q23;
            {var subQ0=sQuery(id+"F0.wireOp",EDGE,"E4");var subQ1=makeQuery(id+"F0.imprint","INTERSECT",VERTEX,{"derivedFrom":[sQuery(id+"F0.wireOp",EDGE,"E2"),subQ0]});Q23=makeQuery(id+"F0.imprint","IMPRINT",FACE,{"disambiguationData":[TD([[makeQuery(id+"F0.imprint","IMPRINT",EDGE,{"disambiguationData":[TD([[subQ1,1.0]])],"derivedFrom":subQ0}),1.0]])]});}
            extrude(context, id + "F2", {"entities" : qUnion([Q0, Q1, Q2, Q3, Q4, Q5, Q6, Q7, Q8, Q9, Q10, Q11, Q12, Q13, Q14, Q15, Q16, Q17, Q18, Q19, Q20, Q21, Q22, Q23]), "operationType" : NewBodyOperationType.REMOVE, "depth" : 1.4 * mm});
        }
        {
            var Q0;
            Q0=makeQuery(id+"F1.opExtrude","CAP_FACE",FACE,{"disambiguationData":[OSD([sQuery(id+"F0.wireOp",EDGE,"E0")])],"isStart":false});
            var sketch = newSketch(context, id + "F3", { "sketchPlane" : qUnion([Q0])});
            skCircle(sketch, "E8", {"center": v(0, 0) * mm, "radius": 13 * mm});
            skCircle(sketch, "E9", {"center": v(0, 0) * mm, "radius": 14.2 * mm});
            skSolve(sketch);
        }
        {
            var Q0;
            Q0=makeQuery(id+"F3.imprint","IMPRINT",FACE,{"disambiguationData":[TD([[makeQuery(id+"F3.imprint","IMPRINT",EDGE,{"derivedFrom":sQuery(id+"F3.wireOp",EDGE,"E9")}),-1.0]])]});
            extrude(context, id + "F4", {"entities" : qUnion([Q0]), "operationType" : NewBodyOperationType.REMOVE, "oppositeDirection" : true, "depth" : 0.7 * mm});
        }
        {
            var Q0;
            Q0=makeQuery(id+"F4.boolean.opBoolean","SPLIT",FACE,{"disambiguationData":[TD([makeQuery(id+"F4.opExtrude","SWEPT_FACE",FACE,{"disambiguationData":[OSD([sQuery(id+"F3.wireOp",EDGE,"E8")])]})])],"derivedFrom":makeQuery(id+"F1.opExtrude","CAP_FACE",FACE,{"disambiguationData":[OSD([sQuery(id+"F0.wireOp",EDGE,"E0")])],"isStart":false})});
            var sketch = newSketch(context, id + "F5", { "sketchPlane" : qUnion([Q0])});
            skCircle(sketch, "E10", {"center": v(0, 0) * mm, "radius": 13 * mm});
            skSolve(sketch);
        }
        {
            var Q0;
            Q0=makeQuery(id+"F5.imprint","IMPRINT",FACE,{"disambiguationData":[TD([[makeQuery(id+"F5.imprint","IMPRINT",EDGE,{"derivedFrom":sQuery(id+"F5.wireOp",EDGE,"E10")}),1.0]])]});
            extrude(context, id + "F6", {"entities" : qUnion([Q0]), "operationType" : NewBodyOperationType.REMOVE, "oppositeDirection" : true, "depth" : 1.3 * mm});
        }
        {
            var Q0;
            Q0=makeQuery(id+"F1.opExtrude","CAP_FACE",FACE,{"disambiguationData":[OSD([sQuery(id+"F0.wireOp",EDGE,"E0")])],"isStart":true});
            var sketch = newSketch(context, id + "F7", { "sketchPlane" : qUnion([Q0])});
            skCircle(sketch, "E11", {"center": v(0, 0) * mm, "radius": 9.5 * mm});
            skSolve(sketch);
        }
        {
            var Q0;
            Q0=makeQuery(id+"F7.imprint","IMPRINT",FACE,{"disambiguationData":[TD([[makeQuery(id+"F7.imprint","IMPRINT",EDGE,{"derivedFrom":sQuery(id+"F7.wireOp",EDGE,"E11")}),1.0]])]});
            extrude(context, id + "F8", {"entities" : qUnion([Q0]), "operationType" : NewBodyOperationType.REMOVE, "oppositeDirection" : true, "depth" : .8 * mm});
        }
        {
            var Q0;
            Q0=makeQuery(id+"F6.boolean.opBoolean","COPY",FACE,{"derivedFrom":makeQuery(id+"F6.opExtrude","CAP_FACE",FACE,{"disambiguationData":[OSD([sQuery(id+"F5.wireOp",EDGE,"E10")])],"isStart":false})});
            chamfer(context, id + "F9", {"entities" : qUnion([Q0]), "width" : .8 * mm, "tangentPropagation" : true});
        }
        {
            var Q0;
            Q0=makeQuery(id+"F8.boolean.opBoolean","COPY",EDGE,{"derivedFrom":makeQuery(id+"F8.opExtrude","CAP_EDGE",EDGE,{"disambiguationData":[OSD([sQuery(id+"F7.wireOp",EDGE,"E11")])],"isStart":false})});
            chamfer(context, id + "F10", {"entities" : qUnion([Q0]), "width" : .8 * mm, "tangentPropagation" : true});
        }
    });
